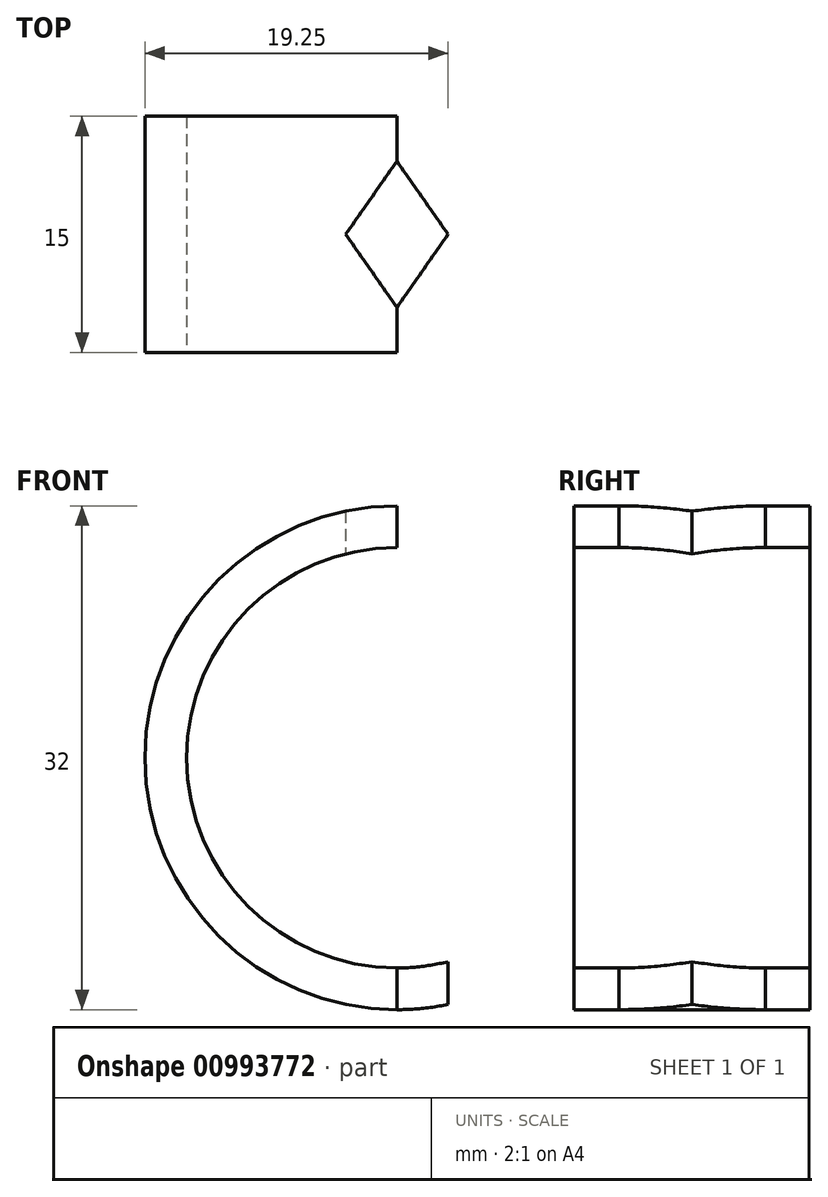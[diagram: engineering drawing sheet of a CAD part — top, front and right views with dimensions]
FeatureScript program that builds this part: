
annotation { "Feature Type Name" : "Feature", "Feature Type Description" : "" }
export const myFeature = defineFeature(function(context is Context, id is Id, definition is map)
    precondition{}
    {
        {
            var Q0;
            Q0=qCreatedBy(makeId("Front.planeOp"),FACE);
            var sketch = newSketch(context, id + "F0", { "sketchPlane" : qUnion([Q0])});
            skCircle(sketch, "E0", {"center": v(0, 0) * mm, "radius": 13.35 * mm});
            skCircle(sketch, "E1", {"center": v(0, 0) * mm, "radius": 16 * mm});
            skSolve(sketch);
        }
        {
            var Q0;
            Q0=makeQuery(id+"F0.imprint","IMPRINT",FACE,{"disambiguationData":[TD([[makeQuery(id+"F0.imprint","IMPRINT",EDGE,{"derivedFrom":sQuery(id+"F0.wireOp",EDGE,"E0")}),-1.0]])]});
            extrude(context, id + "F1", {"entities" : qUnion([Q0]), "oppositeDirection" : true, "depth" : 15 * mm, "offsetDistance" : 25 * mm});
        }
        {
            var Q0;
            Q0=qCreatedBy(makeId("Top.planeOp"),FACE);
            var sketch = newSketch(context, id + "F2", { "sketchPlane" : qUnion([Q0])});
            skLineSegment(sketch, "E2", {"start": v(16, 15) * mm, "end": v(16, 0) * mm});
            skLineSegment(sketch, "E3", {"start": v(0, 15) * mm, "end": v(0, 12.14) * mm});
            skLineSegment(sketch, "E4", {"start": v(0, 12.14) * mm, "end": v(3.25, 7.5) * mm});
            skLineSegment(sketch, "E5", {"start": v(3.25, 7.5) * mm, "end": v(0, 2.86) * mm});
            skLineSegment(sketch, "E6", {"start": v(0, 2.86) * mm, "end": v(0, 0) * mm});
            skLineSegment(sketch, "E7", {"start": v(0, 15) * mm, "end": v(16, 15) * mm});
            skLineSegment(sketch, "E8", {"start": v(16, 0) * mm, "end": v(0, 0) * mm});
            skSolve(sketch);
        }
        {
            var Q0;
            Q0=makeQuery(id+"F2.imprint","IMPRINT",FACE,{"disambiguationData":[TD([[makeQuery(id+"F2.imprint","IMPRINT",EDGE,{"derivedFrom":sQuery(id+"F2.wireOp",EDGE,"E2")}),-1.0]])]});
            extrude(context, id + "F3", {"entities" : qUnion([Q0]), "operationType" : NewBodyOperationType.REMOVE, "oppositeDirection" : true, "depth" : 25 * mm, "offsetDistance" : 25 * mm});
        }
        {
            var Q0;
            Q0=qCreatedBy(makeId("Top.planeOp"),FACE);
            var sketch = newSketch(context, id + "F4", { "sketchPlane" : qUnion([Q0])});
            skLineSegment(sketch, "E9.0", {"start": v(16, 15) * mm, "end": v(16, 0) * mm});
            skLineSegment(sketch, "E10", {"start": v(16, 15) * mm, "end": v(0, 15) * mm});
            skLineSegment(sketch, "E11", {"start": v(0, 15) * mm, "end": v(0, 12.14) * mm});
            skLineSegment(sketch, "E12", {"start": v(0, 12.14) * mm, "end": v(-3.25, 7.5) * mm});
            skLineSegment(sketch, "E13", {"start": v(-3.25, 7.5) * mm, "end": v(0, 2.86) * mm});
            skLineSegment(sketch, "E14", {"start": v(0, 2.86) * mm, "end": v(0, 0) * mm});
            skLineSegment(sketch, "E15", {"start": v(0, 0) * mm, "end": v(16, 0) * mm});
            skSolve(sketch);
        }
        {
            var Q0;
            Q0=makeQuery(id+"F4.imprint","IMPRINT",FACE,{"disambiguationData":[TD([[makeQuery(id+"F4.imprint","IMPRINT",EDGE,{"derivedFrom":sQuery(id+"F4.wireOp",EDGE,"E9.0")}),-1.0]])]});
            extrude(context, id + "F5", {"entities" : qUnion([Q0]), "operationType" : NewBodyOperationType.REMOVE, "depth" : 25 * mm, "offsetDistance" : 25 * mm});
        }
    });
